# Revit family: Grohe_Rainshower_ShowerOutletElbow_(26658DC0)
name_source: partatom
category: Plumbing Fixtures
units: mm (PartAtom-declared; Revit-internal decimal feet)

## family parameters
Cut with Voids When Loaded = No
Host = Face
OmniClass Number = 23.45.05.00
OmniClass Title = Sanitary Equipment
Part Type = Normal
Room Calculation Point = No
Round Connector Dimension = Use Diameter
Shared = No

## types (1)
- RAINSHOWER Shower Outlet Elbow 1/2″ With Holder (26658DC0)
    Assembly Code = D2010
    AssetType = Fixed
    BIMObjectName = Grohe_Rainshower_ShowerOutletElbow_(26658DC0)
    CO2NeutralProduction = GROHE is one of the first leading manufacturer within the sanitary industry having a CO2-neutral production.
    ClassificationName = Uniclass2015
    ClassificationValue = Pr_40_20
    Color = Supersteel
    Cost = 0 $
    Default Elevation = 0 mm  [stored 0 ft]
    Description = RAINSHOWER Shower Outlet Elbow 1/2″ With Holder 26658DC0
    DimensionsDocumentLink = https://cdn.cloud.grohe.com
    DocumentationCertificates = https://www.bimstore.co
    DocumentationInstallationGuide = https://www.bimstore.co
    DocumentationLiterature = https://www.bimstore.co
    DocumentationMaintenance = https://www.bimstore.co
    DocumentationTechnical = https://www.bimstore.co
    DurationUnit = Years
    EF000010 = Wall mounting
    EF002594 = true
    EF002671 = Stainless steel.
    EF006485 = false
    EF021480 = TRUE
    EF021720 = true
    EF022726 = Internal thread
    EF023452 = 1/8 inch
    EF023660 = true
    EF023661 = false
    EF023686 = not applicable
    Ecojoy = No
    ExpectedLife = 0
    FullRecyclabilityOfPlastic = All plastic components are fully recycable
    GROHESocialCommittment = green.grohe.com/social_engagement
    GROHESustainability = green.grohe.com
    IfcExportAs = IfcBuildingElementProxy
    IfcExportType = IfcBuildingElementProxy
    Keynote = N13
    Manufacturer = Grohe
    ManufacturerName = Grohe
    Model = RAINSHOWER Shower Outlet Elbow 1/2″ With Holder 26658DC0
    ModelNumber = 26658DC0
    ModelReference = RAINSHOWER Shower Outlet Elbow 1/2″ With Holder 26658DC0
    NBSDescription = Sanitary fittings and accessories
    NBSObjectName = Grohe - Sanitary fittings and accessories
    NominalDepth = 0 mm  [stored 0 ft]
    NominalHeight = 0 mm  [stored 0 ft]
    NominalLength = 0 mm  [stored 0 ft]
    PrimaryMaterial = Grohe_Supersteel
    ProductDescription = with round escutcheon

Ø 48 mm

male connection thread 1/2"

metal body

protected against backflow

GROHE Long-Life finish
    ProductNumber = 26658DC0
    ProductPageURL = https://www.grohe.co.uk
    ProductShortText = Shower outlet elbow 1/2" with holder
    ProductionYear = 2024
    SustainabilityAward = green.grohe.com/awards
    SustainabilityReport = green.grohe.com/reporting
    TPIDocumentLink = https://cdn.cloud.grohe.com
    Type Comments = RAINSHOWER Shower Outlet Elbow 1/2″ With Holder 26658DC0
    TypeName = RAINSHOWER Shower Outlet Elbow 1/2″ With Holder 26658DC0
    URL = https://www.grohe.co.uk
    WarrantyDurationLabor = 0
    WarrantyDurationParts = 0
    WarrantyDurationUnit = Years
    _BSBibleVersion = 17
    _BimSpecGuid = 0
    _CurrentRevision = 1
    _DistributedBy = https://www.bimstore.co
    _ObjectUserGuide = https://www.bimstore.co

note: [stored X ft] marks values corroborated as IEEE doubles in the binary element streams (Revit-internal decimal feet)

## geometry (parser evidence)
native form markers: Sweep x1
no freeform markers — native parametric forms only
